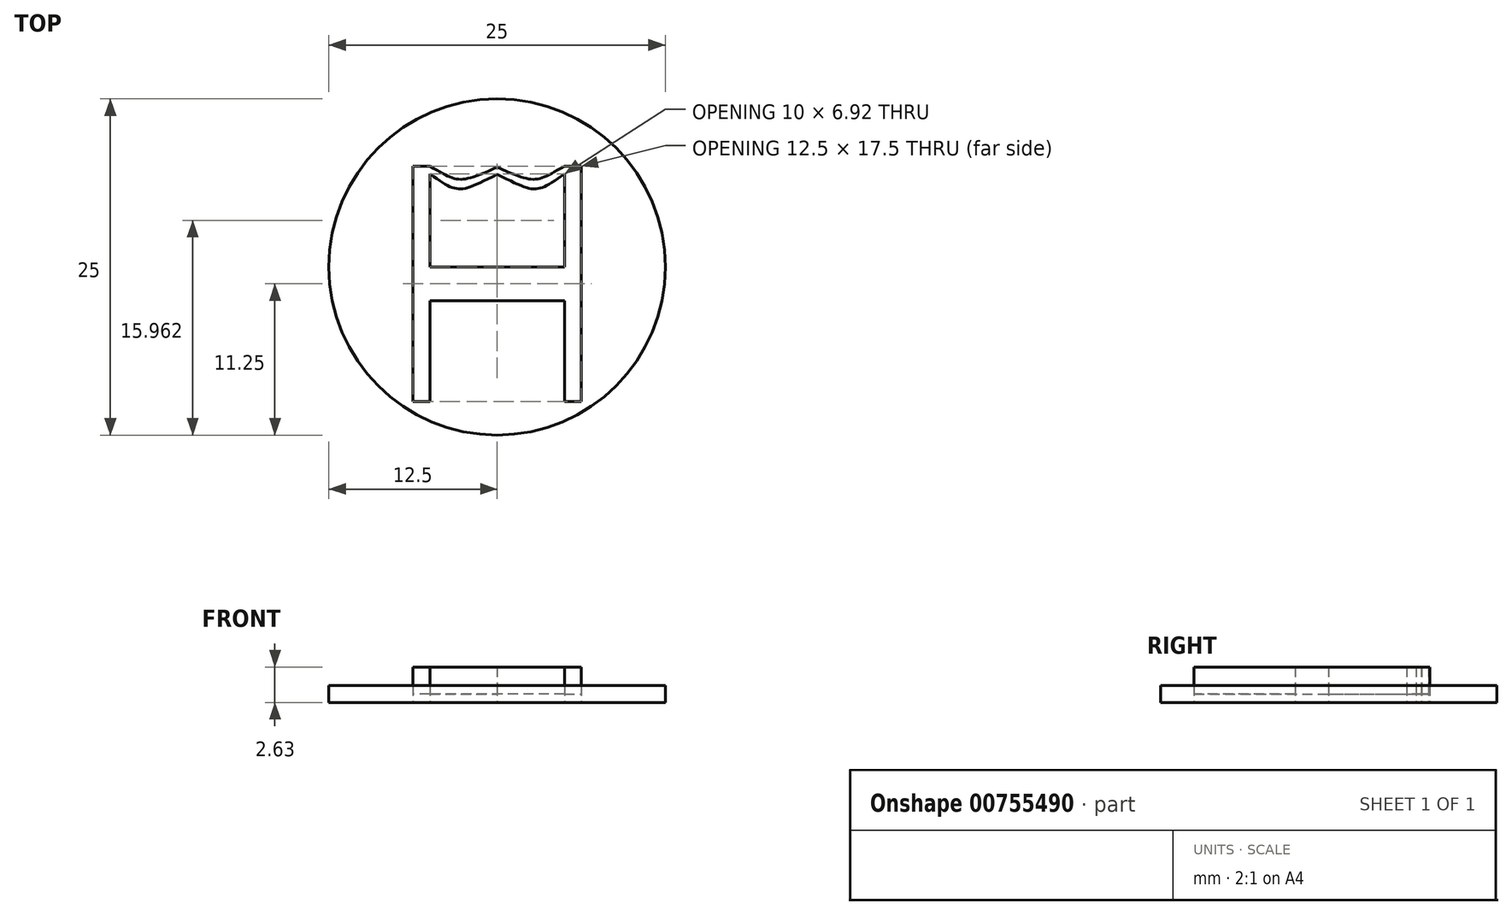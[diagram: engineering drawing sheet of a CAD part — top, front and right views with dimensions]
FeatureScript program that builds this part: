
annotation { "Feature Type Name" : "Feature", "Feature Type Description" : "" }
export const myFeature = defineFeature(function(context is Context, id is Id, definition is map)
    precondition{}
    {
        {
            var Q0;
            Q0=qCreatedBy(makeId("Top.planeOp"),FACE);
            var sketch = newSketch(context, id + "F0", { "sketchPlane" : qUnion([Q0])});
            skCircle(sketch, "E0", {"center": v(0, 0) * mm, "radius": 12.5 * mm});
            skLineSegment(sketch, "E1.bottom", {"start": v(-5, -2.5) * mm, "end": v(-6.25, -2.5) * mm});
            skLineSegment(sketch, "E1.top", {"start": v(-5, -10) * mm, "end": v(-6.25, -10) * mm});
            skLineSegment(sketch, "E1.left", {"start": v(-5, -2.5) * mm, "end": v(-5, -10) * mm});
            skLineSegment(sketch, "E1.right", {"start": v(-6.25, -2.5) * mm, "end": v(-6.25, -10) * mm});
            skLineSegment(sketch, "E2.MirrorCS", {"start": v(6.25, -2.5) * mm, "end": v(6.25, -10) * mm});
            skLineSegment(sketch, "E3.MirrorCS", {"start": v(5, -2.5) * mm, "end": v(6.25, -2.5) * mm});
            skLineSegment(sketch, "E4.MirrorCS", {"start": v(5, -2.5) * mm, "end": v(5, -10) * mm});
            skLineSegment(sketch, "E5.MirrorCS", {"start": v(5, -10) * mm, "end": v(6.25, -10) * mm});
            skLineSegment(sketch, "E6.bottom", {"start": v(6.25, -2.5) * mm, "end": v(-6.25, -2.5) * mm});
            skLineSegment(sketch, "E6.top", {"start": v(6.25, 0) * mm, "end": v(-6.25, 0) * mm});
            skLineSegment(sketch, "E6.left", {"start": v(6.25, -2.5) * mm, "end": v(6.25, 0) * mm});
            skLineSegment(sketch, "E6.right", {"start": v(-6.25, -2.5) * mm, "end": v(-6.25, 0) * mm});
            skLineSegment(sketch, "E7.bottom", {"start": v(-5, 0) * mm, "end": v(-6.25, 0) * mm});
            skLineSegment(sketch, "E7.top", {"start": v(-5, 7.5) * mm, "end": v(-6.25, 7.5) * mm});
            skLineSegment(sketch, "E7.left", {"start": v(-5, 0) * mm, "end": v(-5, 7.5) * mm});
            skLineSegment(sketch, "E7.right", {"start": v(-6.25, 0) * mm, "end": v(-6.25, 7.5) * mm});
            skLineSegment(sketch, "E8.MirrorCS", {"start": v(5, 0) * mm, "end": v(5, 7.5) * mm});
            skLineSegment(sketch, "E9.MirrorCS", {"start": v(6.25, 0) * mm, "end": v(6.25, 7.5) * mm});
            skLineSegment(sketch, "E10.MirrorCS", {"start": v(5, 7.5) * mm, "end": v(6.25, 7.5) * mm});
            skFitSpline(sketch, "E11", {"points": [v(-5, 7.5) * mm, v(0, 7.42) * mm], "startDerivative": vector(6.42, -3.75) * mm, "endDerivative": vector(8.58, 3.8) * mm});
            skFitSpline(sketch, "E12.MirrorCS", {"points": [v(5, 7.5) * mm, v(0, 7.42) * mm], "startDerivative": vector(-6.42, -3.75) * mm, "endDerivative": vector(-8.58, 3.8) * mm});
            skFitSpline(sketch, "E13", {"points": [v(-5, 6.92) * mm, v(0, 6.9) * mm], "startDerivative": vector(6.33, -4.46) * mm, "endDerivative": vector(8.67, 4.37) * mm});
            skFitSpline(sketch, "E14.MirrorCS", {"points": [v(5, 6.92) * mm, v(0, 6.9) * mm], "startDerivative": vector(-6.33, -4.46) * mm, "endDerivative": vector(-8.67, 4.37) * mm});
            skSolve(sketch);
        }
        {
            var Q0;
            {var subQ6=sQuery(id+"F0.wireOp",EDGE,"E13");Q0=makeQuery(id+"F0.imprint","IMPRINT",FACE,{"disambiguationData":[TD([[makeQuery(id+"F0.imprint","IMPRINT",EDGE,{"derivedFrom":subQ6}),-1.0]])]});}
            var Q1;
            Q1=makeQuery(id+"F0.imprint","IMPRINT",FACE,{"disambiguationData":[TD([[makeQuery(id+"F0.imprint","IMPRINT",EDGE,{"derivedFrom":sQuery(id+"F0.wireOp",EDGE,"E0")}),1.0]])]});
            var Q2;
            Q2=qCreatedBy(makeId("Top.planeOp"),FACE);
            extrude(context, id + "F1", {"entities" : qUnion([Q0, Q1]), "endBound" : BoundingType.SYMMETRIC, "depth" : 1.25 * mm, "endBoundEntityFace" : qUnion([Q2]), "offsetDistance" : 25 * mm});
        }
        {
            var Q0;
            Q0=makeQuery(id+"F0.imprint","IMPRINT",FACE,{"disambiguationData":[TD([[makeQuery(id+"F0.imprint","IMPRINT",EDGE,{"derivedFrom":sQuery(id+"F0.wireOp",EDGE,"E1.bottom")}),1.0]])]});
            var Q1;
            Q1=makeQuery(id+"F0.imprint","IMPRINT",FACE,{"disambiguationData":[TD([[makeQuery(id+"F0.imprint","IMPRINT",EDGE,{"derivedFrom":sQuery(id+"F0.wireOp",EDGE,"E1.bottom")}),-1.0]])]});
            var Q2;
            {var subQ1=sQuery(id+"F0.wireOp",EDGE,"E7.top");Q2=makeQuery(id+"F0.imprint","IMPRINT",FACE,{"disambiguationData":[TD([[makeQuery(id+"F0.imprint","IMPRINT",EDGE,{"derivedFrom":subQ1}),1.0]])]});}
            var Q3;
            {var subQ1=sQuery(id+"F0.wireOp",EDGE,"E11");Q3=makeQuery(id+"F0.imprint","IMPRINT",FACE,{"disambiguationData":[TD([[makeQuery(id+"F0.imprint","IMPRINT",EDGE,{"derivedFrom":subQ1}),-1.0]])]});}
            var Q4;
            {var subQ0=sQuery(id+"F0.wireOp",EDGE,"E9.MirrorCS");Q4=makeQuery(id+"F0.imprint","IMPRINT",FACE,{"disambiguationData":[TD([[makeQuery(id+"F0.imprint","IMPRINT",EDGE,{"derivedFrom":subQ0}),1.0]])]});}
            var Q5;
            Q5=makeQuery(id+"F0.imprint","IMPRINT",FACE,{"disambiguationData":[TD([[makeQuery(id+"F0.imprint","IMPRINT",EDGE,{"derivedFrom":sQuery(id+"F0.wireOp",EDGE,"E2.MirrorCS")}),-1.0]])]});
            extrude(context, id + "F2", {"entities" : qUnion([Q0, Q1, Q2, Q3, Q4, Q5]), "depth" : 2 * mm, "offsetDistance" : 25 * mm});
        }
        {
            var Q0;
            Q0=makeQuery(id+"F1.opExtrude","SWEPT_BODY",BODY,{"disambiguationData":[OSD([sQuery(id+"F0.wireOp",EDGE,"E0"),sQuery(id+"F0.wireOp",EDGE,"E1.top"),sQuery(id+"F0.wireOp",EDGE,"E1.left"),sQuery(id+"F0.wireOp",EDGE,"E1.right"),sQuery(id+"F0.wireOp",EDGE,"E2.MirrorCS"),sQuery(id+"F0.wireOp",EDGE,"E4.MirrorCS"),sQuery(id+"F0.wireOp",EDGE,"E5.MirrorCS"),sQuery(id+"F0.wireOp",EDGE,"E6.bottom"),sQuery(id+"F0.wireOp",EDGE,"E6.left"),sQuery(id+"F0.wireOp",EDGE,"E6.right"),sQuery(id+"F0.wireOp",EDGE,"E7.top"),sQuery(id+"F0.wireOp",EDGE,"E7.right"),sQuery(id+"F0.wireOp",EDGE,"E9.MirrorCS"),sQuery(id+"F0.wireOp",EDGE,"E10.MirrorCS"),sQuery(id+"F0.wireOp",EDGE,"E11"),sQuery(id+"F0.wireOp",EDGE,"E12.MirrorCS")])]});
            transform(context, id + "F3", {"entities" : qUnion([Q0]), "transformType" : TransformType.TRANSLATION_3D, "dx" : 30 * mm, "dy" : 0 * mm, "dz" : 0 * mm, "makeCopy" : true});
        }
        {
            var Q0;
            Q0=makeQuery(id+"F3.opPattern","COPY",BODY,{"derivedFrom":makeQuery(id+"F1.opExtrude","SWEPT_BODY",BODY,{"disambiguationData":[OSD([sQuery(id+"F0.wireOp",EDGE,"E0"),sQuery(id+"F0.wireOp",EDGE,"E1.top"),sQuery(id+"F0.wireOp",EDGE,"E1.left"),sQuery(id+"F0.wireOp",EDGE,"E1.right"),sQuery(id+"F0.wireOp",EDGE,"E2.MirrorCS"),sQuery(id+"F0.wireOp",EDGE,"E4.MirrorCS"),sQuery(id+"F0.wireOp",EDGE,"E5.MirrorCS"),sQuery(id+"F0.wireOp",EDGE,"E6.bottom"),sQuery(id+"F0.wireOp",EDGE,"E6.left"),sQuery(id+"F0.wireOp",EDGE,"E6.right"),sQuery(id+"F0.wireOp",EDGE,"E7.top"),sQuery(id+"F0.wireOp",EDGE,"E7.right"),sQuery(id+"F0.wireOp",EDGE,"E9.MirrorCS"),sQuery(id+"F0.wireOp",EDGE,"E10.MirrorCS"),sQuery(id+"F0.wireOp",EDGE,"E11"),sQuery(id+"F0.wireOp",EDGE,"E12.MirrorCS")])]}),"instanceName":"1"});
            deleteBodies(context, id + "F4", {"entities" : qUnion([Q0])});
        }
    });
